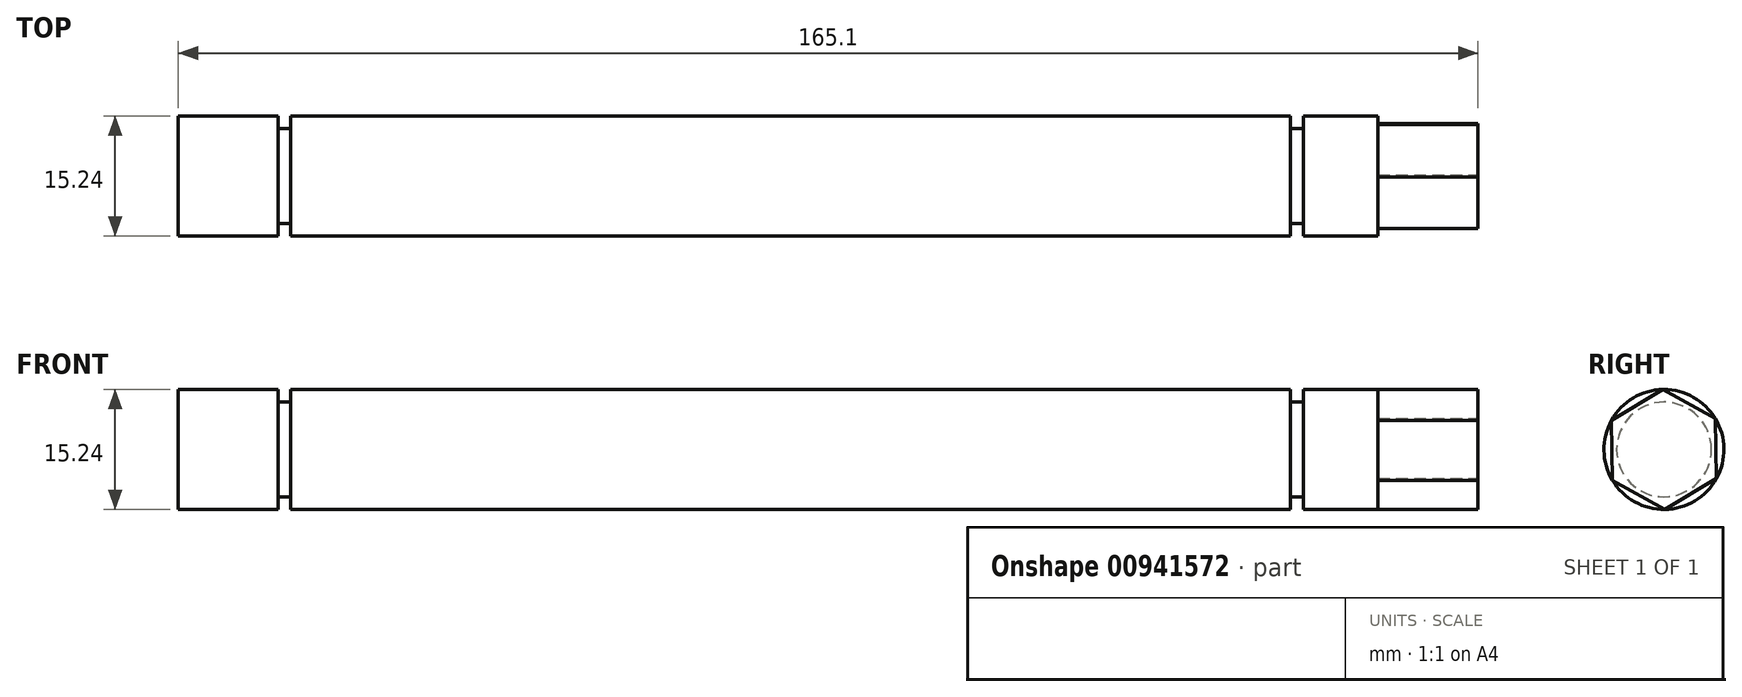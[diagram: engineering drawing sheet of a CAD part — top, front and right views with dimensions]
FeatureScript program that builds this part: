
annotation { "Feature Type Name" : "Feature", "Feature Type Description" : "" }
export const myFeature = defineFeature(function(context is Context, id is Id, definition is map)
    precondition{}
    {
        {
            var Q0;
            Q0=qCreatedBy(makeId("Front.planeOp"),FACE);
            var sketch = newSketch(context, id + "F0", { "sketchPlane" : qUnion([Q0])});
            skLineSegment(sketch, "E0.bottom", {"start": v(0, 0) * mm, "end": v(165.1, 0) * mm});
            skLineSegment(sketch, "E0.top", {"start": v(0, 7.62) * mm, "end": v(12.7, 7.62) * mm});
            skLineSegment(sketch, "E0.left", {"start": v(0, 0) * mm, "end": v(0, 7.62) * mm});
            skLineSegment(sketch, "E0.right", {"start": v(165.1, 0) * mm, "end": v(165.1, 7.62) * mm});
            skLineSegment(sketch, "E1", {"start": v(141.3, 7.62) * mm, "end": v(141.3, 6.02) * mm});
            skLineSegment(sketch, "E2", {"start": v(141.3, 6.02) * mm, "end": v(142.9, 6.02) * mm});
            skLineSegment(sketch, "E3", {"start": v(142.9, 6.02) * mm, "end": v(142.9, 7.62) * mm});
            skLineSegment(sketch, "E4", {"start": v(14.3, 7.62) * mm, "end": v(14.3, 6.02) * mm});
            skLineSegment(sketch, "E5", {"start": v(14.3, 6.02) * mm, "end": v(12.7, 6.02) * mm});
            skLineSegment(sketch, "E6", {"start": v(12.7, 6.02) * mm, "end": v(12.7, 7.62) * mm});
            skLineSegment(sketch, "E7.trimOffspring", {"start": v(14.3, 7.62) * mm, "end": v(141.3, 7.62) * mm});
            skLineSegment(sketch, "E8.trimOffspring", {"start": v(142.9, 7.62) * mm, "end": v(165.1, 7.62) * mm});
            skSolve(sketch);
        }
        {
            var Q0;
            Q0=makeQuery(id+"F0.imprint","IMPRINT",FACE,{"disambiguationData":[TD([[makeQuery(id+"F0.imprint","IMPRINT",EDGE,{"derivedFrom":sQuery(id+"F0.wireOp",EDGE,"E0.bottom")}),1.0]])]});
            var Q1;
            Q1=sQuery(id+"F0.wireOp",EDGE,"E0.bottom");
            revolve(context, id + "F1", {"surfaceOperationType" : NewSurfaceOperationType.NEW, "entities" : qUnion([Q0]), "axis" : qUnion([Q1]), "revolveType" : RevolveType.FULL});
        }
        {
            var Q0;
            Q0=makeQuery(id+"F1.opRevolve","SWEPT_FACE",FACE,{"disambiguationData":[OSD([sQuery(id+"F0.wireOp",EDGE,"E0.right")])]});
            var sketch = newSketch(context, id + "F2", { "sketchPlane" : qUnion([Q0])});
            skCircle(sketch, "E9.cCircle", {"center": v(0, 0) * mm, "radius": 7.62 * mm, "construction": true});
            skLineSegment(sketch, "E9.0", {"start": v(6.54, 3.92) * mm, "end": v(6.66, -3.7) * mm});
            skLineSegment(sketch, "E9.1", {"start": v(6.66, -3.7) * mm, "end": v(0.13, -7.62) * mm});
            skLineSegment(sketch, "E9.2", {"start": v(0.13, -7.62) * mm, "end": v(-6.54, -3.92) * mm});
            skLineSegment(sketch, "E9.3", {"start": v(-6.54, -3.92) * mm, "end": v(-6.66, 3.7) * mm});
            skLineSegment(sketch, "E9.4", {"start": v(-6.66, 3.7) * mm, "end": v(-0.13, 7.62) * mm});
            skLineSegment(sketch, "E9.5", {"start": v(-0.13, 7.62) * mm, "end": v(6.54, 3.92) * mm});
            skSolve(sketch);
        }
        {
            var Q0;
            {var subQ0=sQuery(id+"F2.wireOp",EDGE,"E9.4");Q0=makeQuery(id+"F2.imprint","IMPRINT",FACE,{"disambiguationData":[TD([[makeQuery(id+"F2.imprint","IMPRINT",EDGE,{"derivedFrom":subQ0}),1.0]])]});}
            var Q1;
            {var subQ0=sQuery(id+"F2.wireOp",EDGE,"E9.1");Q1=makeQuery(id+"F2.imprint","IMPRINT",FACE,{"disambiguationData":[TD([[makeQuery(id+"F2.imprint","IMPRINT",EDGE,{"derivedFrom":subQ0}),1.0]])]});}
            var Q2;
            {var subQ0=sQuery(id+"F2.wireOp",EDGE,"E9.2");Q2=makeQuery(id+"F2.imprint","IMPRINT",FACE,{"disambiguationData":[TD([[makeQuery(id+"F2.imprint","IMPRINT",EDGE,{"derivedFrom":subQ0}),1.0]])]});}
            var Q3;
            {var subQ0=sQuery(id+"F2.wireOp",EDGE,"E9.3");Q3=makeQuery(id+"F2.imprint","IMPRINT",FACE,{"disambiguationData":[TD([[makeQuery(id+"F2.imprint","IMPRINT",EDGE,{"derivedFrom":subQ0}),1.0]])]});}
            var Q4;
            {var subQ0=sQuery(id+"F2.wireOp",EDGE,"E9.5");Q4=makeQuery(id+"F2.imprint","IMPRINT",FACE,{"disambiguationData":[TD([[makeQuery(id+"F2.imprint","IMPRINT",EDGE,{"derivedFrom":subQ0}),1.0]])]});}
            var Q5;
            {var subQ0=sQuery(id+"F2.wireOp",EDGE,"E9.0");Q5=makeQuery(id+"F2.imprint","IMPRINT",FACE,{"disambiguationData":[TD([[makeQuery(id+"F2.imprint","IMPRINT",EDGE,{"derivedFrom":subQ0}),1.0]])]});}
            extrude(context, id + "F3", {"entities" : qUnion([Q0, Q1, Q2, Q3, Q4, Q5]), "operationType" : NewBodyOperationType.REMOVE, "oppositeDirection" : true, "depth" : 12.7 * mm, "offsetDistance" : 25.4 * mm});
        }
    });
